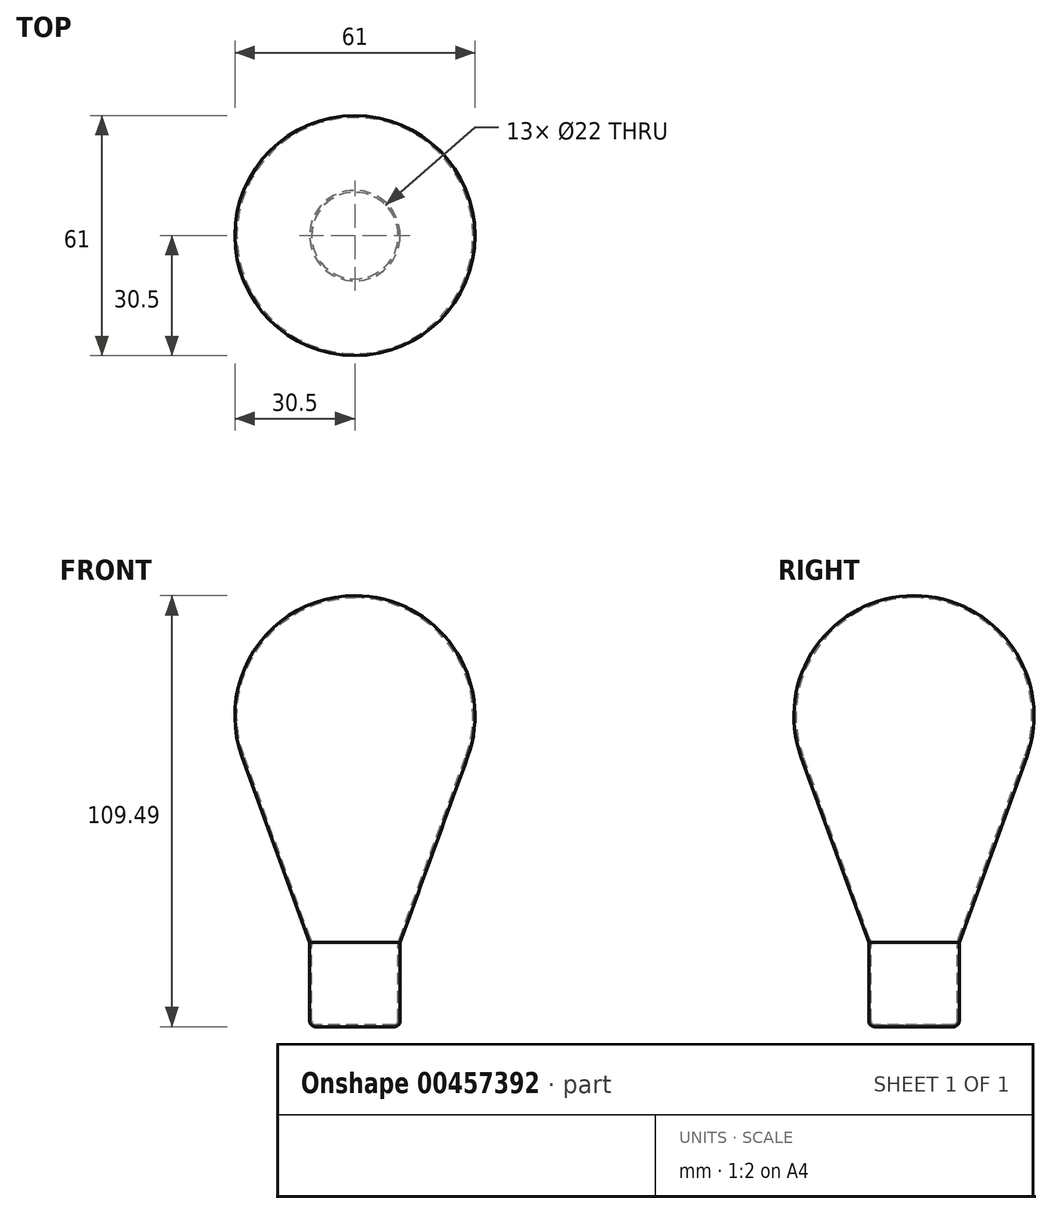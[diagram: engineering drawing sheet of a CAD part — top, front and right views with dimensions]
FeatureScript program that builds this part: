
annotation { "Feature Type Name" : "Feature", "Feature Type Description" : "" }
export const myFeature = defineFeature(function(context is Context, id is Id, definition is map)
    precondition{}
    {
        {
            var Q0;
            Q0=qCreatedBy(makeId("Front.planeOp"),FACE);
            var sketch = newSketch(context, id + "F0", { "sketchPlane" : qUnion([Q0])});
            skArc(sketch, "E0", {"start": v(0, 87.5) * mm, "mid": v(-24.57, 74.7) * mm, "end": v(-28.2, 47.23) * mm});
            skLineSegment(sketch, "E1", {"start": v(0, 0) * mm, "end": v(0, -0.5) * mm});
            skLineSegment(sketch, "E2", {"start": v(-11.3, 0.83) * mm, "end": v(-28.2, 47.23) * mm});
            skLineSegment(sketch, "E3", {"start": v(-11, -0.88) * mm, "end": v(-11, -20) * mm});
            skLineSegment(sketch, "E4", {"start": v(-10, -21) * mm, "end": v(0, -21) * mm});
            skPoint(sketch, "E5.visualSharp", {"position": v(-11, -21) * mm});
            skArc(sketch, "E5.filletArc", {"start": v(-11, -20) * mm, "mid": v(-10.7, -20.7) * mm, "end": v(-10, -21) * mm});
            skPoint(sketch, "E6.visualSharp", {"position": v(-11, 0) * mm});
            skArc(sketch, "E6.filletArc", {"start": v(-11, -0.88) * mm, "mid": v(-11.08, -0.01) * mm, "end": v(-11.3, 0.83) * mm});
            skLineSegment(sketch, "E7.0", {"start": v(-10, -21.5) * mm, "end": v(0, -21.5) * mm});
            skArc(sketch, "E7.1", {"start": v(0, 88) * mm, "mid": v(-24.98, 74.99) * mm, "end": v(-28.66, 47.06) * mm});
            skLineSegment(sketch, "E7.2", {"start": v(-11.5, -0.09) * mm, "end": v(-28.66, 47.06) * mm});
            skLineSegment(sketch, "E7.3", {"start": v(-11.5, -0.09) * mm, "end": v(-11.5, -20) * mm});
            skArc(sketch, "E7.4", {"start": v(-11.5, -20) * mm, "mid": v(-11.06, -21.06) * mm, "end": v(-10, -21.5) * mm});
            skLineSegment(sketch, "E8", {"start": v(0, -21.5) * mm, "end": v(0, -21) * mm});
            skLineSegment(sketch, "E9", {"start": v(0, 88) * mm, "end": v(0, 87.5) * mm});
            skLineSegment(sketch, "E10", {"start": v(-28.66, 47.06) * mm, "end": v(-28.2, 47.23) * mm});
            skLineSegment(sketch, "E11", {"start": v(-11.5, -0.09) * mm, "end": v(-11.09, 0.06) * mm});
            skLineSegment(sketch, "E12", {"start": v(0, 0) * mm, "end": v(0, 88) * mm, "construction": true});
            skLineSegment(sketch, "E13", {"start": v(0, -0.5) * mm, "end": v(0, -21.5) * mm, "construction": true});
            skSolve(sketch);
        }
        {
            var Q0;
            Q0=makeQuery(id+"F0.imprint","IMPRINT",FACE,{"disambiguationData":[TD([[makeQuery(id+"F0.imprint","IMPRINT",EDGE,{"derivedFrom":sQuery(id+"F0.wireOp",EDGE,"E0")}),-1.0]])]});
            var Q1;
            {var subQ1=sQuery(id+"F0.wireOp",EDGE,"E2");Q1=makeQuery(id+"F0.imprint","IMPRINT",FACE,{"disambiguationData":[TD([[makeQuery(id+"F0.imprint","IMPRINT",EDGE,{"derivedFrom":subQ1}),1.0]])]});}
            var Q2;
            {var subQ1=sQuery(id+"F0.wireOp",EDGE,"E3");Q2=makeQuery(id+"F0.imprint","IMPRINT",FACE,{"disambiguationData":[TD([[makeQuery(id+"F0.imprint","IMPRINT",EDGE,{"derivedFrom":subQ1}),-1.0]])]});}
            var Q3;
            Q3=sQuery(id+"F0.wireOp",EDGE,"E13");
            revolve(context, id + "F1", {"entities" : qUnion([Q0, Q1, Q2]), "axis" : qUnion([Q3]), "revolveType" : RevolveType.FULL});
        }
    });
